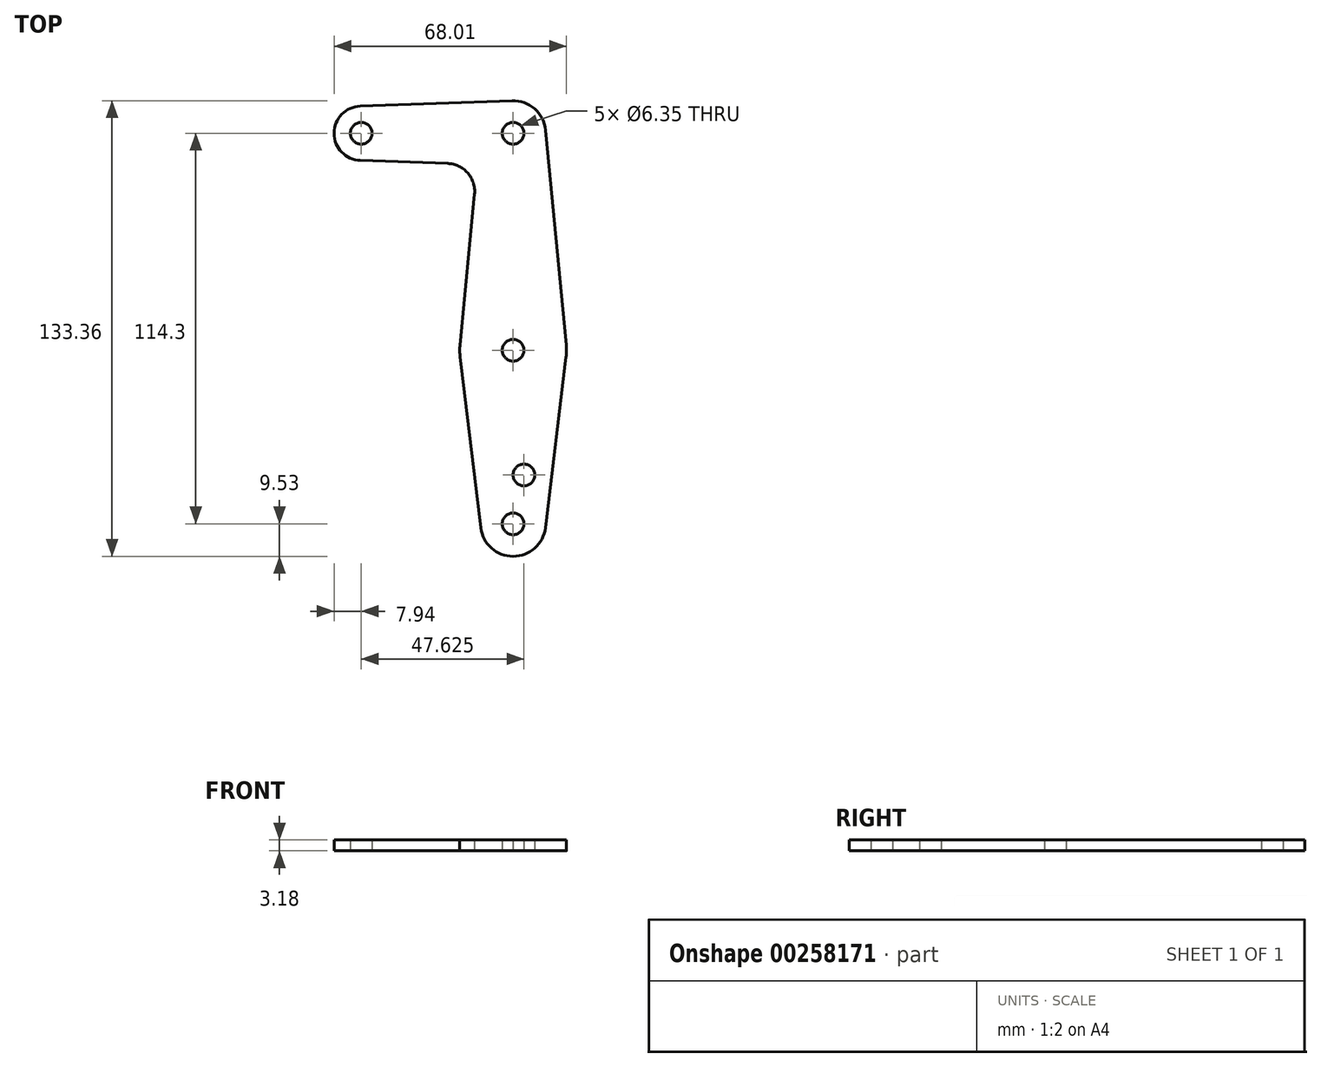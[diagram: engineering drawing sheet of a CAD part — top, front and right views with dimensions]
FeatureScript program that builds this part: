
annotation { "Feature Type Name" : "Feature", "Feature Type Description" : "" }
export const myFeature = defineFeature(function(context is Context, id is Id, definition is map)
    precondition{}
    {
        {
            var Q0;
            Q0=qCreatedBy(makeId("Top.planeOp"),FACE);
            var sketch = newSketch(context, id + "F0", { "sketchPlane" : qUnion([Q0])});
            skCircle(sketch, "E0", {"center": v(0, 0) * mm, "radius": 3.18 * mm});
            skLineSegment(sketch, "E1", {"start": v(0, 0) * mm, "end": v(-44.45, 0) * mm, "construction": true});
            skCircle(sketch, "E2", {"center": v(-44.45, 0) * mm, "radius": 3.18 * mm});
            skCircle(sketch, "E3", {"center": v(-44.45, 0) * mm, "radius": 7.94 * mm});
            skCircle(sketch, "E4", {"center": v(0, 0) * mm, "radius": 9.53 * mm});
            skLineSegment(sketch, "E5", {"start": v(0, 0) * mm, "end": v(0, -63.5) * mm, "construction": true});
            skCircle(sketch, "E6", {"center": v(0, -63.5) * mm, "radius": 3.18 * mm});
            skLineSegment(sketch, "E7", {"start": v(0, -63.5) * mm, "end": v(0, -114.3) * mm, "construction": true});
            skCircle(sketch, "E8", {"center": v(0, -114.3) * mm, "radius": 3.18 * mm});
            skLineSegment(sketch, "E9", {"start": v(0, -63.5) * mm, "end": v(3.18, -63.5) * mm, "construction": true});
            skLineSegment(sketch, "E10", {"start": v(3.18, -63.5) * mm, "end": v(3.18, -100.01) * mm, "construction": true});
            skCircle(sketch, "E11", {"center": v(3.18, -100.01) * mm, "radius": 3.18 * mm});
            skCircle(sketch, "E12", {"center": v(0, -114.3) * mm, "radius": 9.53 * mm});
            skCircle(sketch, "E13", {"center": v(0, -63.5) * mm, "radius": 15.62 * mm});
            skLineSegment(sketch, "E14", {"start": v(9.48, 0.91) * mm, "end": v(15.55, -62) * mm});
            skLineSegment(sketch, "E15", {"start": v(9.46, -115.44) * mm, "end": v(15.5, -65.37) * mm});
            skLineSegment(sketch, "E16", {"start": v(-44.73, -7.93) * mm, "end": v(0, -9.53) * mm});
            skLineSegment(sketch, "E17", {"start": v(-44.73, 7.93) * mm, "end": v(-0.34, 9.52) * mm});
            skLineSegment(sketch, "E18", {"start": v(-9.48, 0.91) * mm, "end": v(-15.55, -62) * mm});
            skLineSegment(sketch, "E19", {"start": v(-15.5, -65.37) * mm, "end": v(-9.46, -115.44) * mm});
            skSolve(sketch);
        }
        {
            var Q0;
            Q0 = qSketchRegion(id + "F0", true);
            extrude(context, id + "F1", {"entities" : qUnion([Q0]), "depth" : 3.17 * mm});
        }
        {
            var Q0;
            Q0=makeQuery(id+"F1.opExtrude","SWEPT_EDGE",EDGE,{"disambiguationData":[OSD([sQuery(id+"F0.wireOp",EDGE,"E16"),sQuery(id+"F0.wireOp",EDGE,"E18")])]});
            fillet(context, id + "F2", {"entities" : qUnion([Q0]), "radius" : 8.2 * mm, "tangentPropagation" : true, "allowEdgeOverflow" : false});
        }
    });
